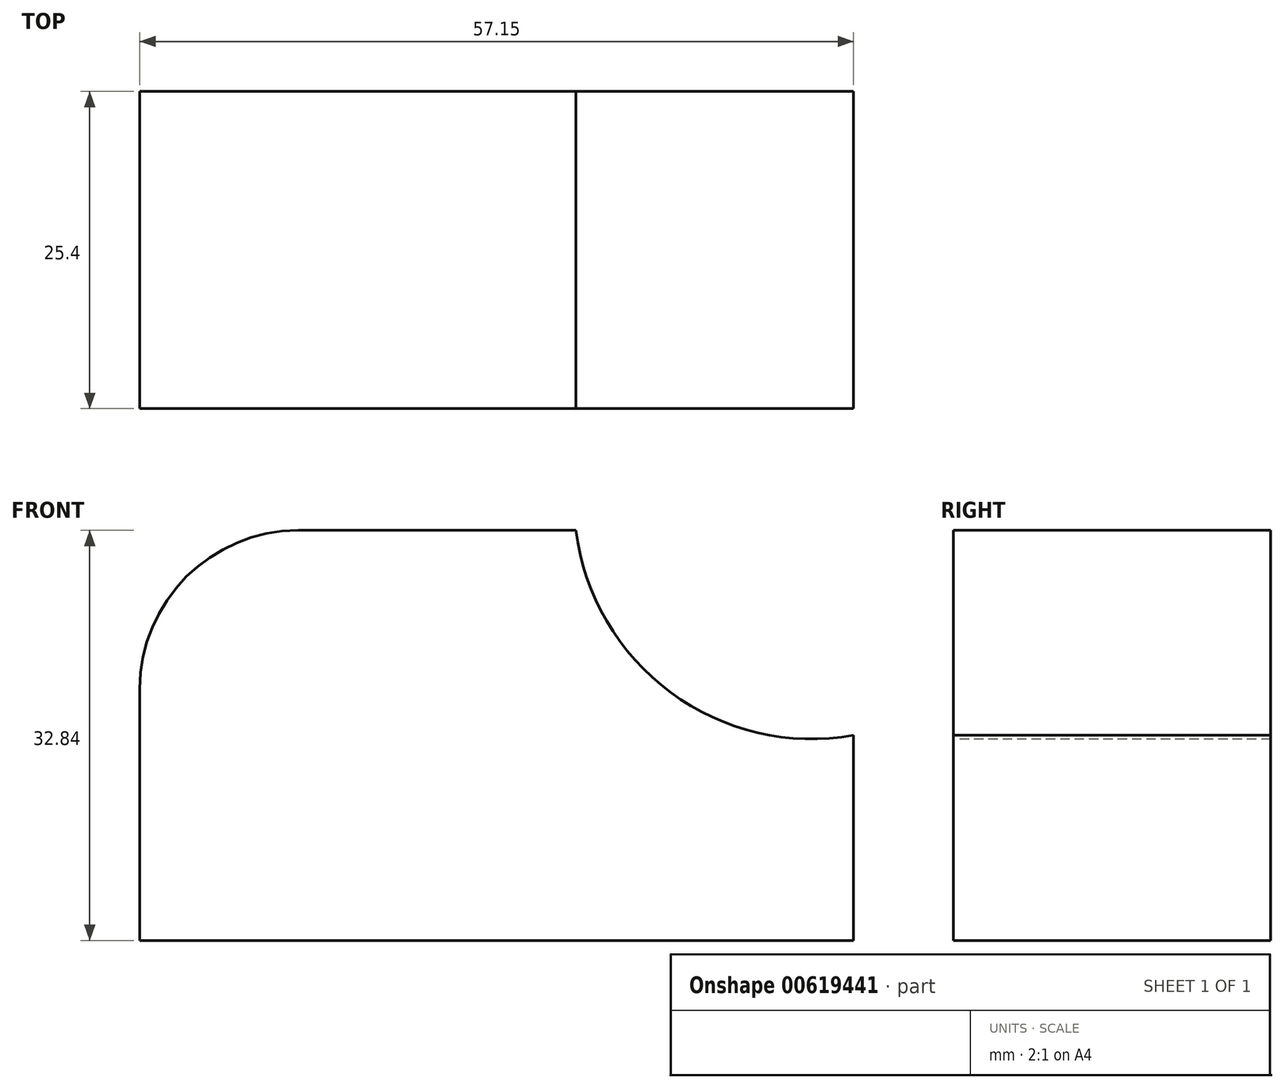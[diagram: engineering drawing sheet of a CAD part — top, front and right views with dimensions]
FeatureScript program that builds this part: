
annotation { "Feature Type Name" : "Feature", "Feature Type Description" : "" }
export const myFeature = defineFeature(function(context is Context, id is Id, definition is map)
    precondition{}
    {
        {
            var Q0;
            Q0=qCreatedBy(makeId("Front.planeOp"),FACE);
            var sketch = newSketch(context, id + "F0", { "sketchPlane" : qUnion([Q0])});
            skLineSegment(sketch, "E0", {"start": v(0, 0) * mm, "end": v(57.15, 0) * mm});
            skLineSegment(sketch, "E1", {"start": v(0, 0) * mm, "end": v(0, 20.14) * mm});
            skLineSegment(sketch, "E2", {"start": v(12.7, 32.84) * mm, "end": v(57.15, 32.84) * mm});
            skLineSegment(sketch, "E3", {"start": v(57.15, 32.84) * mm, "end": v(57.15, 0) * mm});
            skPoint(sketch, "E4.end.orphan", {"position": v(12.7, 32.84) * mm});
            skPoint(sketch, "E5.start.orphan", {"position": v(0, 20.14) * mm});
            skPoint(sketch, "E6.orphan", {"position": v(0, 32.84) * mm});
            skPoint(sketch, "E7.center.orphan", {"position": v(8.98, 23.86) * mm});
            skArc(sketch, "E8", {"start": v(12.7, 32.84) * mm, "mid": v(3.72, 29.12) * mm, "end": v(0, 20.14) * mm});
            skSolve(sketch);
        }
        {
            var Q0;
            Q0 = qSketchRegion(id + "F0", true);
            extrude(context, id + "F1", {"entities" : qUnion([Q0]), "depth" : 25.4 * mm, "offsetDistance" : 25.4 * mm});
        }
        {
            var Q0;
            Q0=makeQuery(id+"F1.opExtrude","CAP_FACE",FACE,{"disambiguationData":[OSD([sQuery(id+"F0.wireOp",EDGE,"E0"),sQuery(id+"F0.wireOp",EDGE,"E1"),sQuery(id+"F0.wireOp",EDGE,"E2"),sQuery(id+"F0.wireOp",EDGE,"E3"),sQuery(id+"F0.wireOp",EDGE,"E8")])],"isStart":false});
            var sketch = newSketch(context, id + "F2", { "sketchPlane" : qUnion([Q0])});
            skArc(sketch, "E9", {"start": v(34.93, 32.84) * mm, "mid": v(42.51, 19.86) * mm, "end": v(57.15, 16.42) * mm});
            skSolve(sketch);
        }
        {
            var Q0;
            {var subQ0=sQuery(id+"F2.wireOp",EDGE,"E9");Q0=makeQuery(id+"F2.imprint","IMPRINT",FACE,{"disambiguationData":[TD([[makeQuery(id+"F2.imprint","IMPRINT",EDGE,{"derivedFrom":subQ0}),1.0]])]});}
            extrude(context, id + "F3", {"entities" : qUnion([Q0]), "operationType" : NewBodyOperationType.REMOVE, "oppositeDirection" : true, "depth" : 25.4 * mm, "offsetDistance" : 25.4 * mm});
        }
    });
